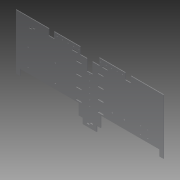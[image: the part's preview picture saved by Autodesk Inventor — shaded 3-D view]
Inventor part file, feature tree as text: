
AUTODESK INVENTOR PART (.ipt)
format: ipt  version: 2014 (Build 180170000, 170)  size: 375,808 bytes
history: native  units: in
note: dims shown in document units (in); Inventor stores cm internally (conversion verified against a paired STEP export)
features: reference x14, extrude x7, sketch x7, projected_geometry x1
ambient origin geometry x8: Origin, YZ Plane, XZ Plane, XY Plane, X Axis, Y Axis, Z Axis, Center Point
bodies: Solid1 (feature_tree)
feature tree (29):
  extrude  "Extrusion1"  Depth=10.125in
  extrude  "Extrusion2"  Depth=1.125in
  extrude  "Extrusion4"  Depth=0.75in
  extrude  "Extrusion5"  Depth=1.0in
  extrude  "Extrusion6"  Depth=6.0in
  extrude  "Extrusion7"  Depth=3.0in
  extrude  "Extrusion8"  Depth=11.5in
  sketch  "Sketch1"  dims[d0=27.0in d1=10.125in]
  sketch  "Sketch2"  dims[d2=0.75in d3=1.125in]
  reference  "Reference1"
  reference  "Reference2"
  reference  "Reference3"
  reference  "Reference4"
  reference  "Reference5"
  reference  "Reference6"
  reference  "Reference7"
  reference  "Reference8"
  reference  "Reference9"
  reference  "Reference10"
  sketch  "Sketch3"  dims[d4=1.125in d5=0.75in]
  projected_geometry  "Projected Loop1"
  reference  "Reference11"
  sketch  "Sketch4"  dims[d6=1.125in d7=1.0in]
  sketch  "Sketch5"  dims[d8=6.0in d9=6.0in]
  reference  "Reference12"
  sketch  "Sketch6"  dims[d10=0.125in d11=0.0in d12=3.0in]
  reference  "Reference13"
  reference  "Reference14"
  sketch  "Sketch7"  dims[d13=4.0in d14=11.5in d15=1.0in d16=0.0in d17=1.0in d18=0.25in d19=1.0in d20=2.0in d21=0.25in d22=0.25in d23=1.0in d24=1.0in d25=0.25in d26=0.25in d27=2.0in d31=3.0in d33=0.125in d34=0.125in d35=0.125in d36=1.0in d37=0.0in d38=1.25in d39=1.25in d40=2.0in d41=1.0in d42=2.0in d43=1.25in d44=4.75in d45=1.0in d46=0.0in d47=0.163in d48=2.3622in d50=1.0in d51=0.3937in d53=1.0in d55=1.0in d56=0.0in d57=0.163in d58=0.163in d59=1.9685in d61=1.0in d62=0.3937in d64=1.0in d66=1.9685in d68=1.0in d69=0.3937in d71=1.0in d73=1.0in d74=0.0in d76=0.25in d77=1.0in d78=0.75in d79=0.75in d80=1.0in d81=1.0in d82=1.0in d83=0.0in]
